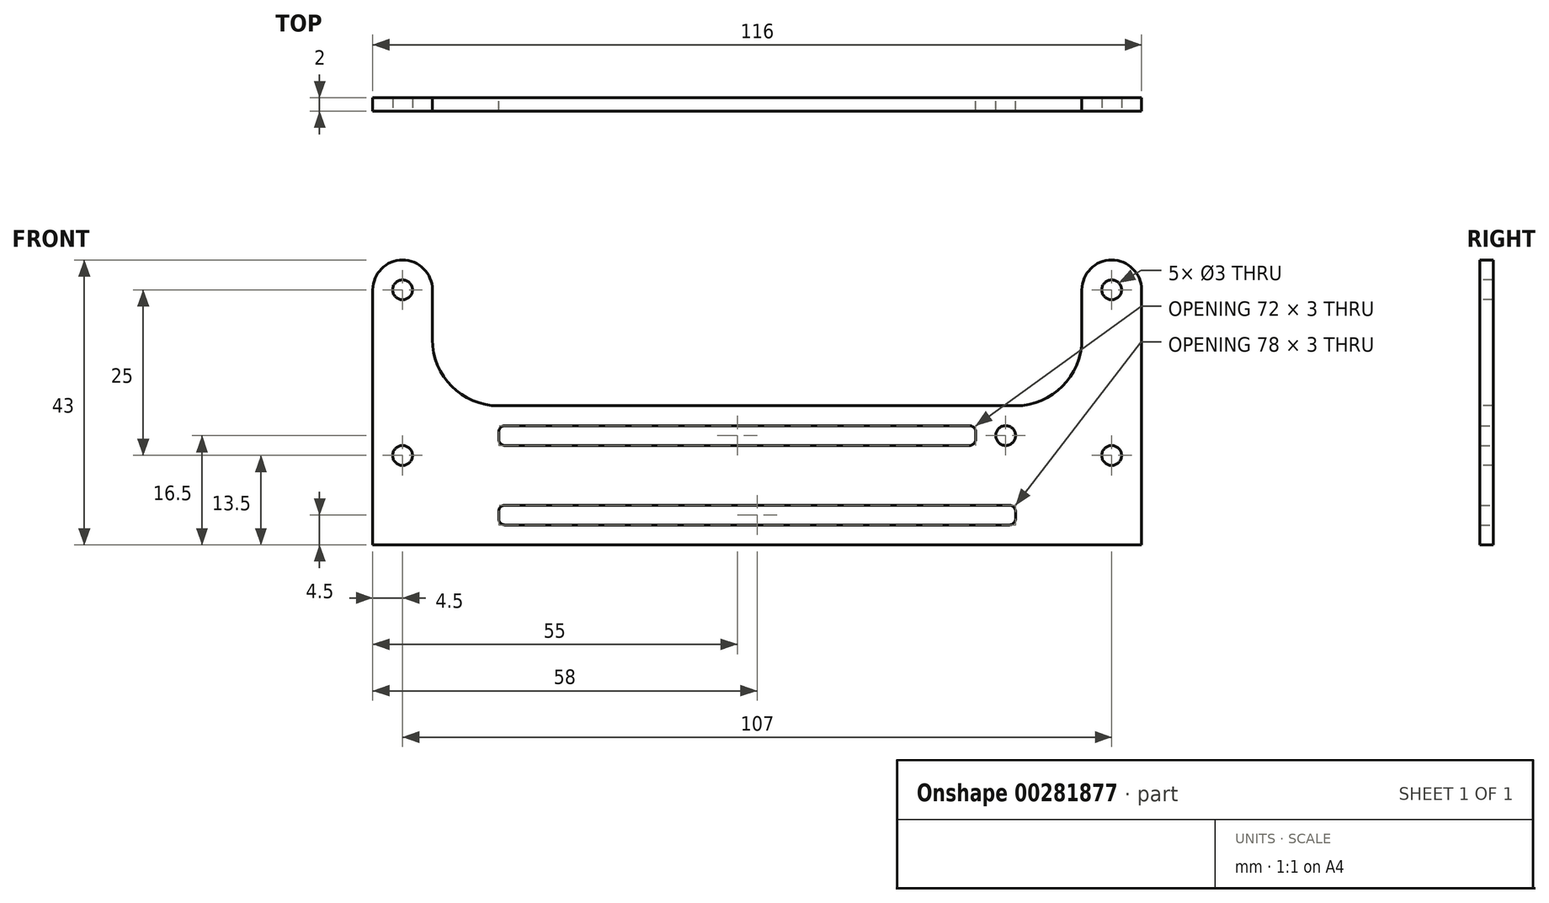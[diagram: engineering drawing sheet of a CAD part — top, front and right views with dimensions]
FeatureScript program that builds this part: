
annotation { "Feature Type Name" : "Feature", "Feature Type Description" : "" }
export const myFeature = defineFeature(function(context is Context, id is Id, definition is map)
    precondition{}
    {
        {
            var Q0;
            Q0=qCreatedBy(makeId("Front.planeOp"),FACE);
            var sketch = newSketch(context, id + "F0", { "sketchPlane" : qUnion([Q0])});
            skLineSegment(sketch, "E0.bottom", {"start": v(42, 10.5) * mm, "end": v(-42, 10.5) * mm});
            skLineSegment(sketch, "E0.top", {"start": v(42, -10.5) * mm, "end": v(-42, -10.5) * mm});
            skLineSegment(sketch, "E0.left", {"start": v(42, 10.5) * mm, "end": v(42, -10.5) * mm});
            skLineSegment(sketch, "E0.right", {"start": v(-42, 10.5) * mm, "end": v(-42, -10.5) * mm});
            skPoint(sketch, "E0.middle", {"position": v(0, 0) * mm});
            skLineSegment(sketch, "E1.bottom", {"start": v(39, -4.5) * mm, "end": v(-39, -4.5) * mm});
            skLineSegment(sketch, "E1.top", {"start": v(39, -7.5) * mm, "end": v(-39, -7.5) * mm});
            skLineSegment(sketch, "E1.left", {"start": v(39, -4.5) * mm, "end": v(39, -7.5) * mm});
            skLineSegment(sketch, "E1.right", {"start": v(-39, -4.5) * mm, "end": v(-39, -7.5) * mm});
            skPoint(sketch, "E1.middle", {"position": v(0, -6) * mm});
            skLineSegment(sketch, "E2.bottom", {"start": v(39, 1.5) * mm, "end": v(-39, 1.5) * mm, "construction": true});
            skLineSegment(sketch, "E2.top", {"start": v(39, -1.5) * mm, "end": v(-39, -1.5) * mm, "construction": true});
            skLineSegment(sketch, "E2.left", {"start": v(39, 1.5) * mm, "end": v(39, -1.5) * mm, "construction": true});
            skLineSegment(sketch, "E2.right", {"start": v(-39, 1.5) * mm, "end": v(-39, -1.5) * mm, "construction": true});
            skLineSegment(sketch, "E3.bottom", {"start": v(-39, 7.5) * mm, "end": v(33, 7.5) * mm});
            skLineSegment(sketch, "E3.top", {"start": v(-39, 4.5) * mm, "end": v(33, 4.5) * mm});
            skLineSegment(sketch, "E3.left", {"start": v(-39, 7.5) * mm, "end": v(-39, 4.5) * mm});
            skLineSegment(sketch, "E3.right", {"start": v(33, 7.5) * mm, "end": v(33, 4.5) * mm});
            skCircle(sketch, "E4", {"center": v(37.5, 6) * mm, "radius": 1.5 * mm});
            skLineSegment(sketch, "E5", {"start": v(0, 0) * mm, "end": v(0, 10.5) * mm, "construction": true});
            skSolve(sketch);
        }
        {
            var Q0;
            Q0=qSketchRegion(id+"F0",true);
            extrude(context, id + "F1", {"entities" : qUnion([Q0]), "depth" : 2 * mm});
        }
        {
            var Q0;
            Q0=makeQuery(id+"F1.opExtrude","SWEPT_EDGE",EDGE,{"disambiguationData":[OSD([sQuery(id+"F0.wireOp",EDGE,"E3.bottom"),sQuery(id+"F0.wireOp",EDGE,"E3.left")])]});
            var Q1;
            Q1=makeQuery(id+"F1.opExtrude","SWEPT_EDGE",EDGE,{"disambiguationData":[OSD([sQuery(id+"F0.wireOp",EDGE,"E2.bottom"),sQuery(id+"F0.wireOp",EDGE,"E2.right")])]});
            var Q2;
            Q2=makeQuery(id+"F1.opExtrude","SWEPT_EDGE",EDGE,{"disambiguationData":[OSD([sQuery(id+"F0.wireOp",EDGE,"E1.bottom"),sQuery(id+"F0.wireOp",EDGE,"E1.right")])]});
            var Q3;
            Q3=makeQuery(id+"F1.opExtrude","SWEPT_EDGE",EDGE,{"disambiguationData":[OSD([sQuery(id+"F0.wireOp",EDGE,"E3.top"),sQuery(id+"F0.wireOp",EDGE,"E3.left")])]});
            var Q4;
            Q4=makeQuery(id+"F1.opExtrude","SWEPT_EDGE",EDGE,{"disambiguationData":[OSD([sQuery(id+"F0.wireOp",EDGE,"E2.top"),sQuery(id+"F0.wireOp",EDGE,"E2.right")])]});
            var Q5;
            Q5=makeQuery(id+"F1.opExtrude","SWEPT_EDGE",EDGE,{"disambiguationData":[OSD([sQuery(id+"F0.wireOp",EDGE,"E1.top"),sQuery(id+"F0.wireOp",EDGE,"E1.right")])]});
            var Q6;
            Q6=makeQuery(id+"F1.opExtrude","SWEPT_EDGE",EDGE,{"disambiguationData":[OSD([sQuery(id+"F0.wireOp",EDGE,"E3.bottom"),sQuery(id+"F0.wireOp",EDGE,"E3.right")])]});
            var Q7;
            Q7=makeQuery(id+"F1.opExtrude","SWEPT_EDGE",EDGE,{"disambiguationData":[OSD([sQuery(id+"F0.wireOp",EDGE,"E2.bottom"),sQuery(id+"F0.wireOp",EDGE,"E2.left")])]});
            var Q8;
            Q8=makeQuery(id+"F1.opExtrude","SWEPT_EDGE",EDGE,{"disambiguationData":[OSD([sQuery(id+"F0.wireOp",EDGE,"E1.bottom"),sQuery(id+"F0.wireOp",EDGE,"E1.left")])]});
            var Q9;
            Q9=makeQuery(id+"F1.opExtrude","SWEPT_EDGE",EDGE,{"disambiguationData":[OSD([sQuery(id+"F0.wireOp",EDGE,"E1.top"),sQuery(id+"F0.wireOp",EDGE,"E1.left")])]});
            var Q10;
            Q10=makeQuery(id+"F1.opExtrude","SWEPT_EDGE",EDGE,{"disambiguationData":[OSD([sQuery(id+"F0.wireOp",EDGE,"E2.top"),sQuery(id+"F0.wireOp",EDGE,"E2.left")])]});
            var Q11;
            Q11=makeQuery(id+"F1.opExtrude","SWEPT_EDGE",EDGE,{"disambiguationData":[OSD([sQuery(id+"F0.wireOp",EDGE,"E3.top"),sQuery(id+"F0.wireOp",EDGE,"E3.right")])]});
            fillet(context, id + "F2", {"entities" : qUnion([Q0, Q1, Q2, Q3, Q4, Q5, Q6, Q7, Q8, Q9, Q10, Q11]), "radius" : 1 * mm, "tangentPropagation" : true, "allowEdgeOverflow" : false});
        }
        {
            var Q0;
            Q0=makeQuery(id+"F1.opExtrude","CAP_FACE",FACE,{"disambiguationData":[OSD([sQuery(id+"F0.wireOp",EDGE,"E0.bottom"),sQuery(id+"F0.wireOp",EDGE,"E0.top"),sQuery(id+"F0.wireOp",EDGE,"E0.left"),sQuery(id+"F0.wireOp",EDGE,"E0.right"),sQuery(id+"F0.wireOp",EDGE,"E1.bottom"),sQuery(id+"F0.wireOp",EDGE,"E1.top"),sQuery(id+"F0.wireOp",EDGE,"E1.left"),sQuery(id+"F0.wireOp",EDGE,"E1.right"),sQuery(id+"F0.wireOp",EDGE,"E2.bottom"),sQuery(id+"F0.wireOp",EDGE,"E2.top"),sQuery(id+"F0.wireOp",EDGE,"E2.left"),sQuery(id+"F0.wireOp",EDGE,"E2.right"),sQuery(id+"F0.wireOp",EDGE,"E3.bottom"),sQuery(id+"F0.wireOp",EDGE,"E3.top"),sQuery(id+"F0.wireOp",EDGE,"E3.left"),sQuery(id+"F0.wireOp",EDGE,"E3.right"),sQuery(id+"F0.wireOp",EDGE,"E4")])],"isStart":false});
            var sketch = newSketch(context, id + "F3", { "sketchPlane" : qUnion([Q0])});
            skLineSegment(sketch, "E6.bottom", {"start": v(53.5, 0) * mm, "end": v(-53.5, 0) * mm});
            skLineSegment(sketch, "E6.top", {"start": v(53.5, 0) * mm, "end": v(-53.5, 0) * mm, "construction": true});
            skLineSegment(sketch, "E6.left", {"start": v(53.5, 0) * mm, "end": v(53.5, 0) * mm});
            skLineSegment(sketch, "E6.right", {"start": v(-53.5, 0) * mm, "end": v(-53.5, 0) * mm});
            skPoint(sketch, "E6.middle", {"position": v(0, 0) * mm});
            skLineSegment(sketch, "E7", {"start": v(37.5, 6) * mm, "end": v(53.5, 6) * mm, "construction": true});
            skLineSegment(sketch, "E8", {"start": v(53.5, 6) * mm, "end": v(53.5, 3) * mm, "construction": true});
            skCircle(sketch, "E9", {"center": v(53.5, 3) * mm, "radius": 1.5 * mm});
            skLineSegment(sketch, "E10", {"start": v(53.5, 3) * mm, "end": v(53.5, 28) * mm, "construction": true});
            skCircle(sketch, "E11", {"center": v(53.5, 28) * mm, "radius": 1.5 * mm});
            skLineSegment(sketch, "E12.bottom", {"start": v(42, -10.5) * mm, "end": v(58, -10.5) * mm});
            skLineSegment(sketch, "E12.top", {"start": v(49, 32.5) * mm, "end": v(58, 32.5) * mm});
            skLineSegment(sketch, "E12.left", {"start": v(42, -10.5) * mm, "end": v(42, 10.5) * mm});
            skLineSegment(sketch, "E12.right", {"start": v(58, -10.5) * mm, "end": v(58, 32.5) * mm});
            skLineSegment(sketch, "E13.top", {"start": v(42, 10.5) * mm, "end": v(49, 10.5) * mm});
            skLineSegment(sketch, "E13.right", {"start": v(49, 32.5) * mm, "end": v(49, 10.5) * mm});
            skLineSegment(sketch, "E14.MirrorCS", {"start": v(-53.5, 6) * mm, "end": v(-53.5, 3) * mm, "construction": true});
            skLineSegment(sketch, "E15.MirrorCS", {"start": v(-53.5, 0) * mm, "end": v(53.5, 0) * mm});
            skLineSegment(sketch, "E16.MirrorCS", {"start": v(-49, 32.5) * mm, "end": v(-49, 10.5) * mm});
            skLineSegment(sketch, "E17.MirrorCS", {"start": v(-42, -10.5) * mm, "end": v(-58, -10.5) * mm});
            skLineSegment(sketch, "E18.MirrorCS", {"start": v(-53.5, 0) * mm, "end": v(53.5, 0) * mm, "construction": true});
            skLineSegment(sketch, "E19.MirrorCS", {"start": v(-58, -10.5) * mm, "end": v(-58, 32.5) * mm});
            skLineSegment(sketch, "E20.MirrorCS", {"start": v(-53.5, 3) * mm, "end": v(-53.5, 28) * mm, "construction": true});
            skCircle(sketch, "E21.MirrorC", {"center": v(-53.5, 28) * mm, "radius": 1.5 * mm});
            skCircle(sketch, "E22.MirrorC", {"center": v(-53.5, 3) * mm, "radius": 1.5 * mm});
            skLineSegment(sketch, "E23.MirrorCS", {"start": v(-37.5, 6) * mm, "end": v(-53.5, 6) * mm, "construction": true});
            skLineSegment(sketch, "E24.MirrorCS", {"start": v(-42, -10.5) * mm, "end": v(-42, 10.5) * mm});
            skLineSegment(sketch, "E25.MirrorCS", {"start": v(-42, 10.5) * mm, "end": v(-49, 10.5) * mm});
            skLineSegment(sketch, "E26.MirrorCS", {"start": v(-49, 32.5) * mm, "end": v(-58, 32.5) * mm});
            skSolve(sketch);
        }
        {
            var Q0;
            Q0=qSketchRegion(id+"F3",true);
            extrude(context, id + "F4", {"entities" : qUnion([Q0]), "operationType" : NewBodyOperationType.ADD, "oppositeDirection" : true, "depth" : 2 * mm});
        }
        {
            var Q0;
            Q0=makeQuery(id+"F4.opExtrude","SWEPT_EDGE",EDGE,{"disambiguationData":[OSD([sQuery(id+"F3.wireOp",EDGE,"E16.MirrorCS"),sQuery(id+"F3.wireOp",EDGE,"E25.MirrorCS")])]});
            var Q1;
            Q1=makeQuery(id+"F4.opExtrude","SWEPT_EDGE",EDGE,{"disambiguationData":[OSD([sQuery(id+"F3.wireOp",EDGE,"E13.top"),sQuery(id+"F3.wireOp",EDGE,"E13.right")])]});
            fillet(context, id + "F5", {"entities" : qUnion([Q0, Q1]), "radius" : 10 * mm, "tangentPropagation" : true, "allowEdgeOverflow" : false});
        }
        {
            var Q0;
            Q0=makeQuery(id+"F4.opExtrude","SWEPT_EDGE",EDGE,{"disambiguationData":[OSD([sQuery(id+"F3.wireOp",EDGE,"E16.MirrorCS"),sQuery(id+"F3.wireOp",EDGE,"E26.MirrorCS")])]});
            var Q1;
            Q1=makeQuery(id+"F4.opExtrude","SWEPT_EDGE",EDGE,{"disambiguationData":[OSD([sQuery(id+"F3.wireOp",EDGE,"E19.MirrorCS"),sQuery(id+"F3.wireOp",EDGE,"E26.MirrorCS")])]});
            var Q2;
            Q2=makeQuery(id+"F4.opExtrude","SWEPT_EDGE",EDGE,{"disambiguationData":[OSD([sQuery(id+"F3.wireOp",EDGE,"E12.top"),sQuery(id+"F3.wireOp",EDGE,"E12.right")])]});
            var Q3;
            Q3=makeQuery(id+"F4.opExtrude","SWEPT_EDGE",EDGE,{"disambiguationData":[OSD([sQuery(id+"F3.wireOp",EDGE,"E12.top"),sQuery(id+"F3.wireOp",EDGE,"E13.right")])]});
            fillet(context, id + "F6", {"entities" : qUnion([Q0, Q1, Q2, Q3]), "radius" : 4.5 * mm, "tangentPropagation" : true, "allowEdgeOverflow" : false});
        }
    });
